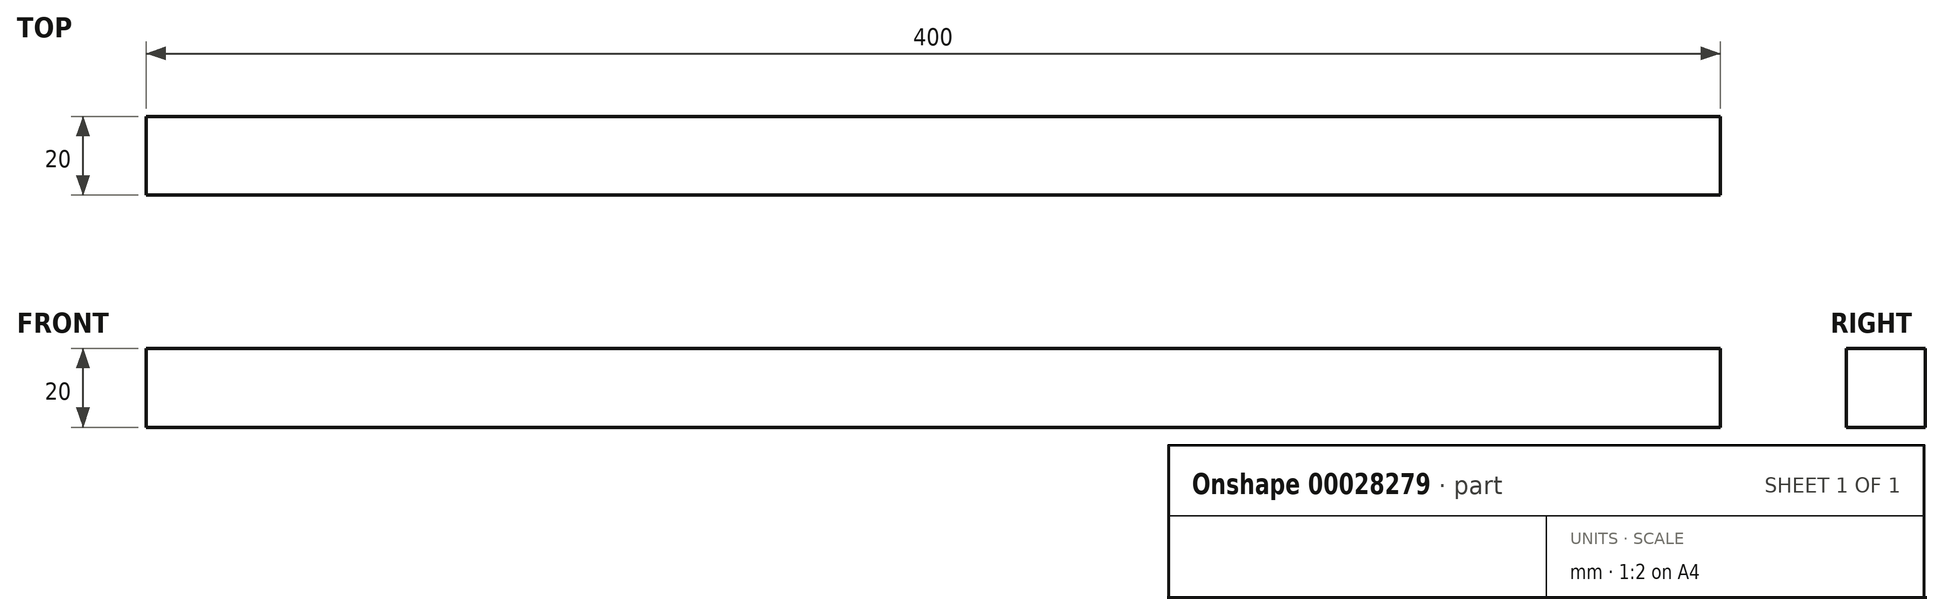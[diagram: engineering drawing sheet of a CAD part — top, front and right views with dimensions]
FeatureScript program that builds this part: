
annotation { "Feature Type Name" : "Feature", "Feature Type Description" : "" }
export const myFeature = defineFeature(function(context is Context, id is Id, definition is map)
    precondition{}
    {
        {
            var Q0;
            Q0=qCreatedBy(makeId("Top.planeOp"),FACE);
            var sketch = newSketch(context, id + "F0", { "sketchPlane" : qUnion([Q0])});
            skLineSegment(sketch, "E0.bottom", {"start": v(0, 0) * mm, "end": v(400, 0) * mm});
            skLineSegment(sketch, "E0.top", {"start": v(0, 20) * mm, "end": v(400, 20) * mm});
            skLineSegment(sketch, "E0.left", {"start": v(0, 0) * mm, "end": v(0, 20) * mm});
            skLineSegment(sketch, "E0.right", {"start": v(400, 0) * mm, "end": v(400, 20) * mm});
            skSolve(sketch);
        }
        {
            var Q0;
            Q0=makeQuery(id+"F0.imprint","IMPRINT",FACE,{"disambiguationData":[TD([[makeQuery(id+"F0.imprint","IMPRINT",EDGE,{"derivedFrom":sQuery(id+"F0.wireOp",EDGE,"E0.bottom")}),1.0]])]});
            extrude(context, id + "F1", {"entities" : qUnion([Q0]), "depth" : 20 * mm});
        }
    });
